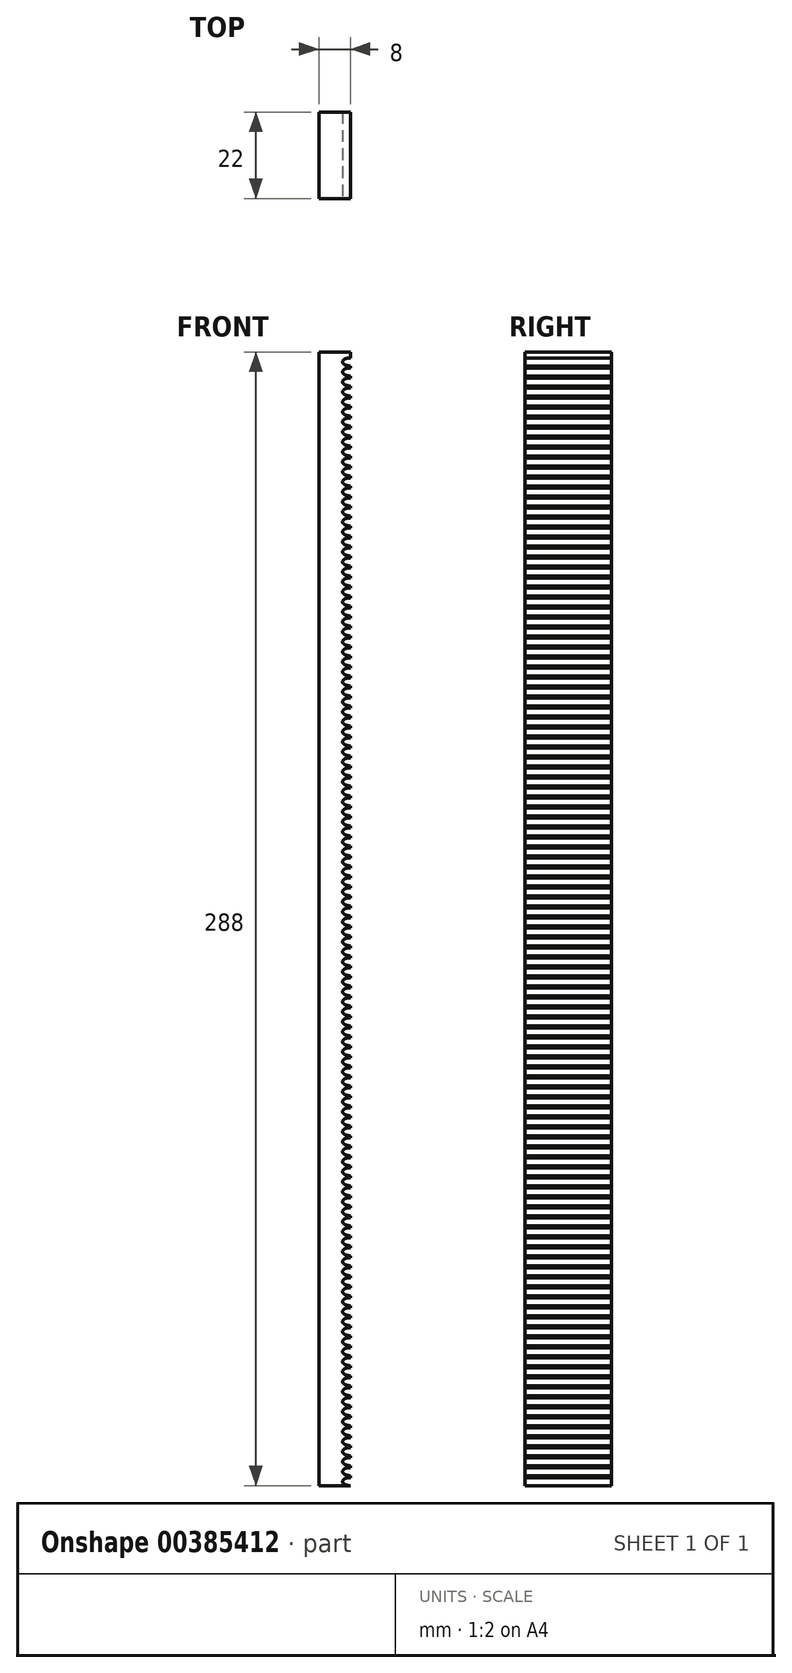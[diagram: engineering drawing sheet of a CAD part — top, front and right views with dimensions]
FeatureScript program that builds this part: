
annotation { "Feature Type Name" : "Feature", "Feature Type Description" : "" }
export const myFeature = defineFeature(function(context is Context, id is Id, definition is map)
    precondition{}
    {
        {
            var Q0;
            Q0=qCreatedBy(makeId("Front.planeOp"),FACE);
            var sketch = newSketch(context, id + "F0", { "sketchPlane" : qUnion([Q0])});
            skLineSegment(sketch, "E0", {"start": v(-44.13, 219.1) * mm, "end": v(-44.13, -68.9) * mm});
            skLineSegment(sketch, "E1", {"start": v(-44.13, -68.9) * mm, "end": v(-36.13, -68.9) * mm});
            skLineSegment(sketch, "E2", {"start": v(-36.13, -68.9) * mm, "end": v(-36.13, 219.1) * mm});
            skLineSegment(sketch, "E3", {"start": v(-36.13, 219.1) * mm, "end": v(-44.13, 219.1) * mm});
            skEllipticalArc(sketch, "E4", {});
            skEllipticalArc(sketch, "E5.0.1.0", {});
            skEllipticalArc(sketch, "E5.0.2.0", {});
            skEllipticalArc(sketch, "E5.0.3.0", {});
            skEllipticalArc(sketch, "E5.0.4.0", {});
            skEllipticalArc(sketch, "E5.0.5.0", {});
            skEllipticalArc(sketch, "E5.0.6.0", {});
            skEllipticalArc(sketch, "E5.0.7.0", {});
            skEllipticalArc(sketch, "E5.0.8.0", {});
            skEllipticalArc(sketch, "E5.0.9.0", {});
            skEllipticalArc(sketch, "E5.0.10.0", {});
            skEllipticalArc(sketch, "E5.0.11.0", {});
            skEllipticalArc(sketch, "E5.0.12.0", {});
            skEllipticalArc(sketch, "E5.0.13.0", {});
            skEllipticalArc(sketch, "E5.0.14.0", {});
            skEllipticalArc(sketch, "E5.0.15.0", {});
            skEllipticalArc(sketch, "E5.0.16.0", {});
            skEllipticalArc(sketch, "E5.0.17.0", {});
            skEllipticalArc(sketch, "E5.0.18.0", {});
            skEllipticalArc(sketch, "E5.0.19.0", {});
            skEllipticalArc(sketch, "E5.0.20.0", {});
            skEllipticalArc(sketch, "E5.0.21.0", {});
            skEllipticalArc(sketch, "E5.0.22.0", {});
            skEllipticalArc(sketch, "E5.0.23.0", {});
            skEllipticalArc(sketch, "E5.0.24.0", {});
            skEllipticalArc(sketch, "E5.0.25.0", {});
            skEllipticalArc(sketch, "E5.0.26.0", {});
            skEllipticalArc(sketch, "E5.0.27.0", {});
            skEllipticalArc(sketch, "E5.0.28.0", {});
            skEllipticalArc(sketch, "E5.0.29.0", {});
            skEllipticalArc(sketch, "E5.0.30.0", {});
            skEllipticalArc(sketch, "E5.0.31.0", {});
            skEllipticalArc(sketch, "E5.0.32.0", {});
            skEllipticalArc(sketch, "E5.0.33.0", {});
            skEllipticalArc(sketch, "E5.0.34.0", {});
            skEllipticalArc(sketch, "E5.0.35.0", {});
            skEllipticalArc(sketch, "E5.0.36.0", {});
            skEllipticalArc(sketch, "E5.0.37.0", {});
            skEllipticalArc(sketch, "E5.0.38.0", {});
            skEllipticalArc(sketch, "E5.0.39.0", {});
            skEllipticalArc(sketch, "E5.0.40.0", {});
            skEllipticalArc(sketch, "E5.0.41.0", {});
            skEllipticalArc(sketch, "E5.0.42.0", {});
            skEllipticalArc(sketch, "E5.0.43.0", {});
            skEllipticalArc(sketch, "E5.0.44.0", {});
            skEllipticalArc(sketch, "E5.0.45.0", {});
            skEllipticalArc(sketch, "E5.0.46.0", {});
            skEllipticalArc(sketch, "E5.0.47.0", {});
            skEllipticalArc(sketch, "E5.0.48.0", {});
            skEllipticalArc(sketch, "E5.0.49.0", {});
            skEllipticalArc(sketch, "E5.0.50.0", {});
            skEllipticalArc(sketch, "E5.0.51.0", {});
            skEllipticalArc(sketch, "E5.0.52.0", {});
            skEllipticalArc(sketch, "E5.0.53.0", {});
            skEllipticalArc(sketch, "E5.0.54.0", {});
            skEllipticalArc(sketch, "E5.0.55.0", {});
            skEllipticalArc(sketch, "E5.0.56.0", {});
            skEllipticalArc(sketch, "E5.0.57.0", {});
            skEllipticalArc(sketch, "E5.0.58.0", {});
            skEllipticalArc(sketch, "E5.0.59.0", {});
            skEllipticalArc(sketch, "E5.0.60.0", {});
            skEllipticalArc(sketch, "E5.0.61.0", {});
            skEllipticalArc(sketch, "E5.0.62.0", {});
            skEllipticalArc(sketch, "E5.0.63.0", {});
            skEllipticalArc(sketch, "E5.0.64.0", {});
            skEllipticalArc(sketch, "E5.0.65.0", {});
            skEllipticalArc(sketch, "E5.0.66.0", {});
            skEllipticalArc(sketch, "E5.0.67.0", {});
            skEllipticalArc(sketch, "E5.0.68.0", {});
            skEllipticalArc(sketch, "E5.0.69.0", {});
            skEllipticalArc(sketch, "E5.0.70.0", {});
            skEllipticalArc(sketch, "E5.0.71.0", {});
            skEllipticalArc(sketch, "E5.0.72.0", {});
            skEllipticalArc(sketch, "E5.0.73.0", {});
            skEllipticalArc(sketch, "E5.0.74.0", {});
            skEllipticalArc(sketch, "E5.0.75.0", {});
            skEllipticalArc(sketch, "E5.0.76.0", {});
            skEllipticalArc(sketch, "E5.0.77.0", {});
            skEllipticalArc(sketch, "E5.0.78.0", {});
            skEllipticalArc(sketch, "E5.0.79.0", {});
            skEllipticalArc(sketch, "E5.0.80.0", {});
            skEllipticalArc(sketch, "E5.0.81.0", {});
            skEllipticalArc(sketch, "E5.0.82.0", {});
            skEllipticalArc(sketch, "E5.0.83.0", {});
            skEllipticalArc(sketch, "E5.0.84.0", {});
            skEllipticalArc(sketch, "E5.0.85.0", {});
            skEllipticalArc(sketch, "E5.0.86.0", {});
            skEllipticalArc(sketch, "E5.0.87.0", {});
            skEllipticalArc(sketch, "E5.0.88.0", {});
            skEllipticalArc(sketch, "E5.0.89.0", {});
            skEllipticalArc(sketch, "E5.0.90.0", {});
            skEllipticalArc(sketch, "E5.0.91.0", {});
            skEllipticalArc(sketch, "E5.0.92.0", {});
            skEllipticalArc(sketch, "E5.0.93.0", {});
            skEllipticalArc(sketch, "E5.0.94.0", {});
            skEllipticalArc(sketch, "E5.0.95.0", {});
            skEllipticalArc(sketch, "E5.0.96.0", {});
            skEllipticalArc(sketch, "E5.0.97.0", {});
            skEllipticalArc(sketch, "E5.0.98.0", {});
            skEllipticalArc(sketch, "E5.0.99.0", {});
            skLineSegment(sketch, "E5.direction1", {"start": v(-36.13, -68.9) * mm, "end": v(-10.73, -68.9) * mm, "construction": true});
            skLineSegment(sketch, "E5.direction2", {"start": v(-36.13, -68.9) * mm, "end": v(-36.13, -66.36) * mm, "construction": true});
            skEllipticalArc(sketch, "E6.0.1.0", {});
            skEllipticalArc(sketch, "E6.0.2.0", {});
            skEllipticalArc(sketch, "E6.0.3.0", {});
            skEllipticalArc(sketch, "E6.0.4.0", {});
            skEllipticalArc(sketch, "E6.0.5.0", {});
            skEllipticalArc(sketch, "E6.0.6.0", {});
            skEllipticalArc(sketch, "E6.0.7.0", {});
            skEllipticalArc(sketch, "E6.0.8.0", {});
            skEllipticalArc(sketch, "E6.0.9.0", {});
            skEllipticalArc(sketch, "E6.0.10.0", {});
            skEllipticalArc(sketch, "E6.0.11.0", {});
            skEllipticalArc(sketch, "E6.0.12.0", {});
            skEllipticalArc(sketch, "E6.0.13.0", {});
            skLineSegment(sketch, "E6.direction1", {"start": v(-36.13, 182.56) * mm, "end": v(-10.73, 182.56) * mm, "construction": true});
            skLineSegment(sketch, "E6.direction2", {"start": v(-36.13, 182.56) * mm, "end": v(-36.13, 185.1) * mm, "construction": true});
            const initialGuessF0  = {"E4": [-0.03613029750904212, -0.06788785335107533, 1, 0, 0.0019939000000000003, 0.001016, 1.5707963267948966, 4.71238898038469], "E5.0.1.0": [-0.03613029750904212, -0.06534785331322639, 1, 0, 0.0019939000000000003, 0.001016, 1.5707963267948966, 4.71238898038469], "E5.0.2.0": [-0.03613029750904212, -0.06280785327537744, 1, 0, 0.0019939000000000003, 0.001016, 1.5707963267948966, 4.71238898038469], "E5.0.3.0": [-0.03613029750904212, -0.06026785323752849, 1, 0, 0.0019939000000000003, 0.001016, 1.5707963267948966, 4.71238898038469], "E5.0.4.0": [-0.03613029750904212, -0.057727853199679546, 1, 0, 0.0019939000000000003, 0.001016, 1.5707963267948966, 4.71238898038469], "E5.0.5.0": [-0.03613029750904212, -0.0551878531618306, 1, 0, 0.0019939000000000003, 0.001016, 1.5707963267948966, 4.71238898038469], "E5.0.6.0": [-0.03613029750904212, -0.05264785312398165, 1, 0, 0.0019939000000000003, 0.001016, 1.5707963267948966, 4.71238898038469], "E5.0.7.0": [-0.03613029750904212, -0.050107853086132706, 1, 0, 0.0019939000000000003, 0.001016, 1.5707963267948966, 4.71238898038469], "E5.0.8.0": [-0.03613029750904212, -0.04756785304828376, 1, 0, 0.0019939000000000003, 0.001016, 1.5707963267948966, 4.71238898038469], "E5.0.9.0": [-0.03613029750904212, -0.04502785301043481, 1, 0, 0.0019939000000000003, 0.001016, 1.5707963267948966, 4.71238898038469], "E5.0.10.0": [-0.03613029750904212, -0.042487852972585866, 1, 0, 0.0019939000000000003, 0.001016, 1.5707963267948966, 4.71238898038469], "E5.0.11.0": [-0.03613029750904212, -0.03994785293473692, 1, 0, 0.0019939000000000003, 0.001016, 1.5707963267948966, 4.71238898038469], "E5.0.12.0": [-0.03613029750904212, -0.03740785289688797, 1, 0, 0.0019939000000000003, 0.001016, 1.5707963267948966, 4.71238898038469], "E5.0.13.0": [-0.03613029750904212, -0.034867852859039025, 1, 0, 0.0019939000000000003, 0.001016, 1.5707963267948966, 4.71238898038469], "E5.0.14.0": [-0.03613029750904212, -0.03232785282119008, 1, 0, 0.0019939000000000003, 0.001016, 1.5707963267948966, 4.71238898038469], "E5.0.15.0": [-0.03613029750904212, -0.02978785278334113, 1, 0, 0.0019939000000000003, 0.001016, 1.5707963267948966, 4.71238898038469], "E5.0.16.0": [-0.03613029750904212, -0.027247852745492185, 1, 0, 0.0019939000000000003, 0.001016, 1.5707963267948966, 4.71238898038469], "E5.0.17.0": [-0.03613029750904212, -0.024707852707643238, 1, 0, 0.0019939000000000003, 0.001016, 1.5707963267948966, 4.71238898038469], "E5.0.18.0": [-0.03613029750904212, -0.02216785266979429, 1, 0, 0.0019939000000000003, 0.001016, 1.5707963267948966, 4.71238898038469], "E5.0.19.0": [-0.03613029750904212, -0.019627852631945344, 1, 0, 0.0019939000000000003, 0.001016, 1.5707963267948966, 4.71238898038469], "E5.0.20.0": [-0.03613029750904212, -0.017087852594096398, 1, 0, 0.0019939000000000003, 0.001016, 1.5707963267948966, 4.71238898038469], "E5.0.21.0": [-0.03613029750904212, -0.014547852556247451, 1, 0, 0.0019939000000000003, 0.001016, 1.5707963267948966, 4.71238898038469], "E5.0.22.0": [-0.03613029750904212, -0.012007852518398504, 1, 0, 0.0019939000000000003, 0.001016, 1.5707963267948966, 4.71238898038469], "E5.0.23.0": [-0.03613029750904212, -0.009467852480549557, 1, 0, 0.0019939000000000003, 0.001016, 1.5707963267948966, 4.71238898038469], "E5.0.24.0": [-0.03613029750904212, -0.0069278524427006105, 1, 0, 0.0019939000000000003, 0.001016, 1.5707963267948966, 4.71238898038469], "E5.0.25.0": [-0.03613029750904212, -0.004387852404851664, 1, 0, 0.0019939000000000003, 0.001016, 1.5707963267948966, 4.71238898038469], "E5.0.26.0": [-0.03613029750904212, -0.001847852367002717, 1, 0, 0.0019939000000000003, 0.001016, 1.5707963267948966, 4.71238898038469], "E5.0.27.0": [-0.03613029750904212, 0.0006921476708462299, 1, 0, 0.0019939000000000003, 0.001016, 1.5707963267948966, 4.71238898038469], "E5.0.28.0": [-0.03613029750904212, 0.0032321477086951766, 1, 0, 0.0019939000000000003, 0.001016, 1.5707963267948966, 4.71238898038469], "E5.0.29.0": [-0.03613029750904212, 0.0057721477465441234, 1, 0, 0.0019939000000000003, 0.001016, 1.5707963267948966, 4.71238898038469], "E5.0.30.0": [-0.03613029750904212, 0.00831214778439307, 1, 0, 0.0019939000000000003, 0.001016, 1.5707963267948966, 4.71238898038469], "E5.0.31.0": [-0.03613029750904212, 0.010852147822242017, 1, 0, 0.0019939000000000003, 0.001016, 1.5707963267948966, 4.71238898038469], "E5.0.32.0": [-0.03613029750904212, 0.013392147860090964, 1, 0, 0.0019939000000000003, 0.001016, 1.5707963267948966, 4.71238898038469], "E5.0.33.0": [-0.03613029750904212, 0.01593214789793991, 1, 0, 0.0019939000000000003, 0.001016, 1.5707963267948966, 4.71238898038469], "E5.0.34.0": [-0.03613029750904212, 0.018472147935788857, 1, 0, 0.0019939000000000003, 0.001016, 1.5707963267948966, 4.71238898038469], "E5.0.35.0": [-0.03613029750904212, 0.021012147973637804, 1, 0, 0.0019939000000000003, 0.001016, 1.5707963267948966, 4.71238898038469], "E5.0.36.0": [-0.03613029750904212, 0.02355214801148675, 1, 0, 0.0019939000000000003, 0.001016, 1.5707963267948966, 4.71238898038469], "E5.0.37.0": [-0.03613029750904212, 0.026092148049335698, 1, 0, 0.0019939000000000003, 0.001016, 1.5707963267948966, 4.71238898038469], "E5.0.38.0": [-0.03613029750904212, 0.028632148087184645, 1, 0, 0.0019939000000000003, 0.001016, 1.5707963267948966, 4.71238898038469], "E5.0.39.0": [-0.03613029750904212, 0.03117214812503359, 1, 0, 0.0019939000000000003, 0.001016, 1.5707963267948966, 4.71238898038469], "E5.0.40.0": [-0.03613029750904212, 0.03371214816288254, 1, 0, 0.0019939000000000003, 0.001016, 1.5707963267948966, 4.71238898038469], "E5.0.41.0": [-0.03613029750904212, 0.036252148200731485, 1, 0, 0.0019939000000000003, 0.001016, 1.5707963267948966, 4.71238898038469], "E5.0.42.0": [-0.03613029750904212, 0.03879214823858043, 1, 0, 0.0019939000000000003, 0.001016, 1.5707963267948966, 4.71238898038469], "E5.0.43.0": [-0.03613029750904212, 0.04133214827642938, 1, 0, 0.0019939000000000003, 0.001016, 1.5707963267948966, 4.71238898038469], "E5.0.44.0": [-0.03613029750904212, 0.043872148314278325, 1, 0, 0.0019939000000000003, 0.001016, 1.5707963267948966, 4.71238898038469], "E5.0.45.0": [-0.03613029750904212, 0.04641214835212727, 1, 0, 0.0019939000000000003, 0.001016, 1.5707963267948966, 4.71238898038469], "E5.0.46.0": [-0.03613029750904212, 0.04895214838997622, 1, 0, 0.0019939000000000003, 0.001016, 1.5707963267948966, 4.71238898038469], "E5.0.47.0": [-0.03613029750904212, 0.051492148427825166, 1, 0, 0.0019939000000000003, 0.001016, 1.5707963267948966, 4.71238898038469], "E5.0.48.0": [-0.03613029750904212, 0.05403214846567411, 1, 0, 0.0019939000000000003, 0.001016, 1.5707963267948966, 4.71238898038469], "E5.0.49.0": [-0.03613029750904212, 0.05657214850352306, 1, 0, 0.0019939000000000003, 0.001016, 1.5707963267948966, 4.71238898038469], "E5.0.50.0": [-0.03613029750904212, 0.059112148541372006, 1, 0, 0.0019939000000000003, 0.001016, 1.5707963267948966, 4.71238898038469], "E5.0.51.0": [-0.03613029750904212, 0.06165214857922097, 1, 0, 0.0019939000000000003, 0.001016, 1.5707963267948966, 4.71238898038469], "E5.0.52.0": [-0.03613029750904212, 0.0641921486170699, 1, 0, 0.0019939000000000003, 0.001016, 1.5707963267948966, 4.71238898038469], "E5.0.53.0": [-0.03613029750904212, 0.06673214865491883, 1, 0, 0.0019939000000000003, 0.001016, 1.5707963267948966, 4.71238898038469], "E5.0.54.0": [-0.03613029750904212, 0.0692721486927678, 1, 0, 0.0019939000000000003, 0.001016, 1.5707963267948966, 4.71238898038469], "E5.0.55.0": [-0.03613029750904212, 0.07181214873061675, 1, 0, 0.0019939000000000003, 0.001016, 1.5707963267948966, 4.71238898038469], "E5.0.56.0": [-0.03613029750904212, 0.07435214876846569, 1, 0, 0.0019939000000000003, 0.001016, 1.5707963267948966, 4.71238898038469], "E5.0.57.0": [-0.03613029750904212, 0.07689214880631462, 1, 0, 0.0019939000000000003, 0.001016, 1.5707963267948966, 4.71238898038469], "E5.0.58.0": [-0.03613029750904212, 0.07943214884416358, 1, 0, 0.0019939000000000003, 0.001016, 1.5707963267948966, 4.71238898038469], "E5.0.59.0": [-0.03613029750904212, 0.08197214888201254, 1, 0, 0.0019939000000000003, 0.001016, 1.5707963267948966, 4.71238898038469], "E5.0.60.0": [-0.03613029750904212, 0.08451214891986147, 1, 0, 0.0019939000000000003, 0.001016, 1.5707963267948966, 4.71238898038469], "E5.0.61.0": [-0.03613029750904212, 0.0870521489577104, 1, 0, 0.0019939000000000003, 0.001016, 1.5707963267948966, 4.71238898038469], "E5.0.62.0": [-0.03613029750904212, 0.08959214899555937, 1, 0, 0.0019939000000000003, 0.001016, 1.5707963267948966, 4.71238898038469], "E5.0.63.0": [-0.03613029750904212, 0.09213214903340833, 1, 0, 0.0019939000000000003, 0.001016, 1.5707963267948966, 4.71238898038469], "E5.0.64.0": [-0.03613029750904212, 0.09467214907125726, 1, 0, 0.0019939000000000003, 0.001016, 1.5707963267948966, 4.71238898038469], "E5.0.65.0": [-0.03613029750904212, 0.0972121491091062, 1, 0, 0.0019939000000000003, 0.001016, 1.5707963267948966, 4.71238898038469], "E5.0.66.0": [-0.03613029750904212, 0.09975214914695515, 1, 0, 0.0019939000000000003, 0.001016, 1.5707963267948966, 4.71238898038469], "E5.0.67.0": [-0.03613029750904212, 0.10229214918480412, 1, 0, 0.0019939000000000003, 0.001016, 1.5707963267948966, 4.71238898038469], "E5.0.68.0": [-0.03613029750904212, 0.10483214922265305, 1, 0, 0.0019939000000000003, 0.001016, 1.5707963267948966, 4.71238898038469], "E5.0.69.0": [-0.03613029750904212, 0.10737214926050198, 1, 0, 0.0019939000000000003, 0.001016, 1.5707963267948966, 4.71238898038469], "E5.0.70.0": [-0.03613029750904212, 0.10991214929835094, 1, 0, 0.0019939000000000003, 0.001016, 1.5707963267948966, 4.71238898038469], "E5.0.71.0": [-0.03613029750904212, 0.1124521493361999, 1, 0, 0.0019939000000000003, 0.001016, 1.5707963267948966, 4.71238898038469], "E5.0.72.0": [-0.03613029750904212, 0.11499214937404884, 1, 0, 0.0019939000000000003, 0.001016, 1.5707963267948966, 4.71238898038469], "E5.0.73.0": [-0.03613029750904212, 0.11753214941189777, 1, 0, 0.0019939000000000003, 0.001016, 1.5707963267948966, 4.71238898038469], "E5.0.74.0": [-0.03613029750904212, 0.12007214944974673, 1, 0, 0.0019939000000000003, 0.001016, 1.5707963267948966, 4.71238898038469], "E5.0.75.0": [-0.03613029750904212, 0.12261214948759569, 1, 0, 0.0019939000000000003, 0.001016, 1.5707963267948966, 4.71238898038469], "E5.0.76.0": [-0.03613029750904212, 0.12515214952544462, 1, 0, 0.0019939000000000003, 0.001016, 1.5707963267948966, 4.71238898038469], "E5.0.77.0": [-0.03613029750904212, 0.12769214956329356, 1, 0, 0.0019939000000000003, 0.001016, 1.5707963267948966, 4.71238898038469], "E5.0.78.0": [-0.03613029750904212, 0.13023214960114252, 1, 0, 0.0019939000000000003, 0.001016, 1.5707963267948966, 4.71238898038469], "E5.0.79.0": [-0.03613029750904212, 0.13277214963899148, 1, 0, 0.0019939000000000003, 0.001016, 1.5707963267948966, 4.71238898038469], "E5.0.80.0": [-0.03613029750904212, 0.1353121496768404, 1, 0, 0.0019939000000000003, 0.001016, 1.5707963267948966, 4.71238898038469], "E5.0.81.0": [-0.03613029750904212, 0.13785214971468934, 1, 0, 0.0019939000000000003, 0.001016, 1.5707963267948966, 4.71238898038469], "E5.0.82.0": [-0.03613029750904212, 0.1403921497525383, 1, 0, 0.0019939000000000003, 0.001016, 1.5707963267948966, 4.71238898038469], "E5.0.83.0": [-0.03613029750904212, 0.14293214979038726, 1, 0, 0.0019939000000000003, 0.001016, 1.5707963267948966, 4.71238898038469], "E5.0.84.0": [-0.03613029750904212, 0.1454721498282362, 1, 0, 0.0019939000000000003, 0.001016, 1.5707963267948966, 4.71238898038469], "E5.0.85.0": [-0.03613029750904212, 0.14801214986608513, 1, 0, 0.0019939000000000003, 0.001016, 1.5707963267948966, 4.71238898038469], "E5.0.86.0": [-0.03613029750904212, 0.1505521499039341, 1, 0, 0.0019939000000000003, 0.001016, 1.5707963267948966, 4.71238898038469], "E5.0.87.0": [-0.03613029750904212, 0.15309214994178305, 1, 0, 0.0019939000000000003, 0.001016, 1.5707963267948966, 4.71238898038469], "E5.0.88.0": [-0.03613029750904212, 0.15563214997963198, 1, 0, 0.0019939000000000003, 0.001016, 1.5707963267948966, 4.71238898038469], "E5.0.89.0": [-0.03613029750904212, 0.15817215001748092, 1, 0, 0.0019939000000000003, 0.001016, 1.5707963267948966, 4.71238898038469], "E5.0.90.0": [-0.03613029750904212, 0.16071215005532988, 1, 0, 0.0019939000000000003, 0.001016, 1.5707963267948966, 4.71238898038469], "E5.0.91.0": [-0.03613029750904212, 0.16325215009317884, 1, 0, 0.0019939000000000003, 0.001016, 1.5707963267948966, 4.71238898038469], "E5.0.92.0": [-0.03613029750904212, 0.16579215013102777, 1, 0, 0.0019939000000000003, 0.001016, 1.5707963267948966, 4.71238898038469], "E5.0.93.0": [-0.03613029750904212, 0.1683321501688767, 1, 0, 0.0019939000000000003, 0.001016, 1.5707963267948966, 4.71238898038469], "E5.0.94.0": [-0.03613029750904212, 0.17087215020672566, 1, 0, 0.0019939000000000003, 0.001016, 1.5707963267948966, 4.71238898038469], "E5.0.95.0": [-0.03613029750904212, 0.17341215024457463, 1, 0, 0.0019939000000000003, 0.001016, 1.5707963267948966, 4.71238898038469], "E5.0.96.0": [-0.03613029750904212, 0.17595215028242356, 1, 0, 0.0019939000000000003, 0.001016, 1.5707963267948966, 4.71238898038469], "E5.0.97.0": [-0.03613029750904212, 0.1784921503202725, 1, 0, 0.0019939000000000003, 0.001016, 1.5707963267948966, 4.71238898038469], "E5.0.98.0": [-0.03613029750904212, 0.18103215035812145, 1, 0, 0.0019939000000000003, 0.001016, 1.5707963267948966, 4.71238898038469], "E5.0.99.0": [-0.03613029750904212, 0.1835721503959704, 1, 0, 0.0019939000000000003, 0.001016, 1.5707963267948966, 4.71238898038469], "E6.0.1.0": [-0.03613029750904212, 0.18611215043381937, 1, 0, 0.0019939000000000003, 0.001016, 1.5707963267948966, 4.71238898038469], "E6.0.2.0": [-0.03613029750904212, 0.18865215047166833, 1, 0, 0.0019939000000000003, 0.001016, 1.5707963267948966, 4.71238898038469], "E6.0.3.0": [-0.03613029750904212, 0.1911921505095173, 1, 0, 0.0019939000000000003, 0.001016, 1.5707963267948966, 4.71238898038469], "E6.0.4.0": [-0.03613029750904212, 0.19373215054736626, 1, 0, 0.0019939000000000003, 0.001016, 1.5707963267948966, 4.71238898038469], "E6.0.5.0": [-0.03613029750904212, 0.19627215058521522, 1, 0, 0.0019939000000000003, 0.001016, 1.5707963267948966, 4.71238898038469], "E6.0.6.0": [-0.03613029750904212, 0.19881215062306418, 1, 0, 0.0019939000000000003, 0.001016, 1.5707963267948966, 4.71238898038469], "E6.0.7.0": [-0.03613029750904212, 0.20135215066091314, 1, 0, 0.0019939000000000003, 0.001016, 1.5707963267948966, 4.71238898038469], "E6.0.8.0": [-0.03613029750904212, 0.2038921506987621, 1, 0, 0.0019939000000000003, 0.001016, 1.5707963267948966, 4.71238898038469], "E6.0.9.0": [-0.03613029750904212, 0.20643215073661106, 1, 0, 0.0019939000000000003, 0.001016, 1.5707963267948966, 4.71238898038469], "E6.0.10.0": [-0.03613029750904212, 0.20897215077446002, 1, 0, 0.0019939000000000003, 0.001016, 1.5707963267948966, 4.71238898038469], "E6.0.11.0": [-0.03613029750904212, 0.21151215081230898, 1, 0, 0.0019939000000000003, 0.001016, 1.5707963267948966, 4.71238898038469], "E6.0.12.0": [-0.03613029750904212, 0.21405215085015794, 1, 0, 0.0019939000000000003, 0.001016, 1.5707963267948966, 4.71238898038469], "E6.0.13.0": [-0.03613029750904212, 0.2165921508880069, 1, 0, 0.0019939000000000003, 0.001016, 1.5707963267948966, 4.71238898038469]};
            skSetInitialGuess(sketch, initialGuessF0);
            skSolve(sketch);
        }
        {
            var Q0;
            Q0=makeQuery(id+"F0.imprint","IMPRINT",FACE,{"disambiguationData":[TD([[makeQuery(id+"F0.imprint","IMPRINT",EDGE,{"derivedFrom":sQuery(id+"F0.wireOp",EDGE,"E0")}),1.0]])]});
            extrude(context, id + "F1", {"entities" : qUnion([Q0]), "oppositeDirection" : true, "depth" : 22 * mm});
        }
    });
